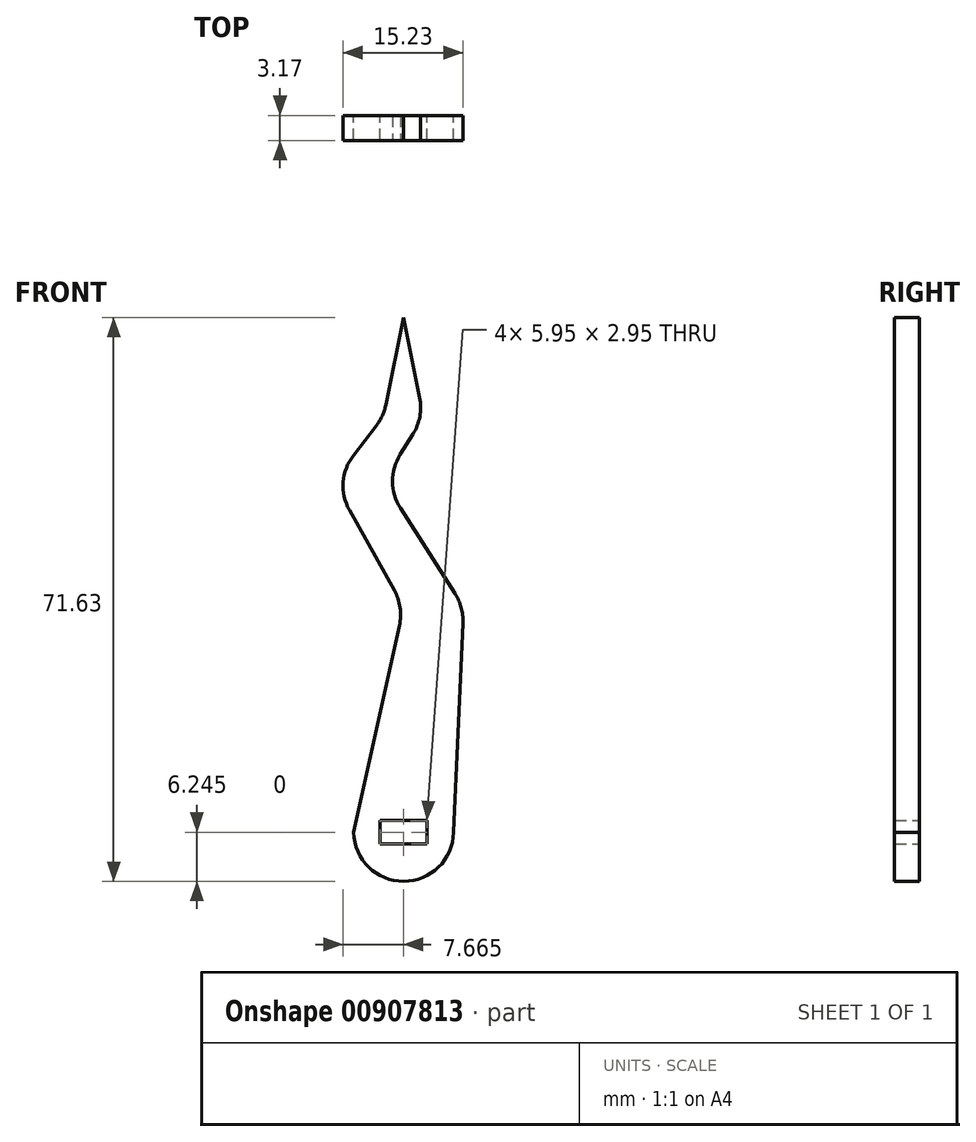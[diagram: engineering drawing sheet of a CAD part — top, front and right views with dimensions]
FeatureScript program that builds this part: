
annotation { "Feature Type Name" : "Feature", "Feature Type Description" : "" }
export const myFeature = defineFeature(function(context is Context, id is Id, definition is map)
    precondition{}
    {
        {
            var Q0;
            Q0=qCreatedBy(makeId("Front.planeOp"),FACE);
            var sketch = newSketch(context, id + "F0", { "sketchPlane" : qUnion([Q0])});
            skLineSegment(sketch, "E0.bottom", {"start": v(-3, 1.5) * mm, "end": v(2.95, 1.5) * mm});
            skLineSegment(sketch, "E0.top", {"start": v(-3, -1.45) * mm, "end": v(2.95, -1.45) * mm});
            skLineSegment(sketch, "E0.left", {"start": v(-3, 1.5) * mm, "end": v(-3, -1.45) * mm});
            skLineSegment(sketch, "E0.right", {"start": v(2.95, 1.5) * mm, "end": v(2.95, -1.45) * mm});
            skArc(sketch, "E1", {"start": v(-6.35, 0) * mm, "mid": v(0, -6.22) * mm, "end": v(6.35, 0) * mm});
            skLineSegment(sketch, "E2", {"start": v(-6.35, 0) * mm, "end": v(0, 28.64) * mm});
            skLineSegment(sketch, "E3", {"start": v(0, 28.64) * mm, "end": v(-8.92, 44.6) * mm});
            skLineSegment(sketch, "E4", {"start": v(-8.92, 44.6) * mm, "end": v(-2.54, 52.89) * mm});
            skLineSegment(sketch, "E5", {"start": v(-2.54, 52.89) * mm, "end": v(0, 65.41) * mm});
            skLineSegment(sketch, "E6", {"start": v(0, 65.41) * mm, "end": v(2.54, 52.74) * mm});
            skLineSegment(sketch, "E7", {"start": v(2.54, 52.74) * mm, "end": v(-2.57, 44.6) * mm});
            skLineSegment(sketch, "E8", {"start": v(-2.57, 44.6) * mm, "end": v(7.62, 28.64) * mm});
            skLineSegment(sketch, "E9", {"start": v(7.62, 28.64) * mm, "end": v(6.35, 0) * mm});
            skSolve(sketch);
        }
        {
            var Q0;
            Q0 = qSketchRegion(id + "F0", true);
            extrude(context, id + "F1", {"entities" : qUnion([Q0]), "depth" : 3.17 * mm, "offsetDistance" : 25.4 * mm});
        }
        {
            var Q0;
            Q0=makeQuery(id+"F1.opExtrude","SWEPT_EDGE",EDGE,{"disambiguationData":[OSD([sQuery(id+"F0.wireOp",EDGE,"E6"),sQuery(id+"F0.wireOp",EDGE,"E7")])]});
            var Q1;
            Q1=makeQuery(id+"F1.opExtrude","SWEPT_EDGE",EDGE,{"disambiguationData":[OSD([sQuery(id+"F0.wireOp",EDGE,"E7"),sQuery(id+"F0.wireOp",EDGE,"E8")])]});
            var Q2;
            Q2=makeQuery(id+"F1.opExtrude","SWEPT_EDGE",EDGE,{"disambiguationData":[OSD([sQuery(id+"F0.wireOp",EDGE,"E8"),sQuery(id+"F0.wireOp",EDGE,"E9")])]});
            var Q3;
            Q3=makeQuery(id+"F1.opExtrude","SWEPT_EDGE",EDGE,{"disambiguationData":[OSD([sQuery(id+"F0.wireOp",EDGE,"E2"),sQuery(id+"F0.wireOp",EDGE,"E3")])]});
            var Q4;
            Q4=makeQuery(id+"F1.opExtrude","SWEPT_EDGE",EDGE,{"disambiguationData":[OSD([sQuery(id+"F0.wireOp",EDGE,"E3"),sQuery(id+"F0.wireOp",EDGE,"E4")])]});
            var Q5;
            Q5=makeQuery(id+"F1.opExtrude","SWEPT_EDGE",EDGE,{"disambiguationData":[OSD([sQuery(id+"F0.wireOp",EDGE,"E4"),sQuery(id+"F0.wireOp",EDGE,"E5")])]});
            fillet(context, id + "F2", {"entities" : qUnion([Q0, Q1, Q2, Q3, Q4, Q5]), "radius" : 6.35 * mm, "tangentPropagation" : true, "allowEdgeOverflow" : false});
        }
    });
